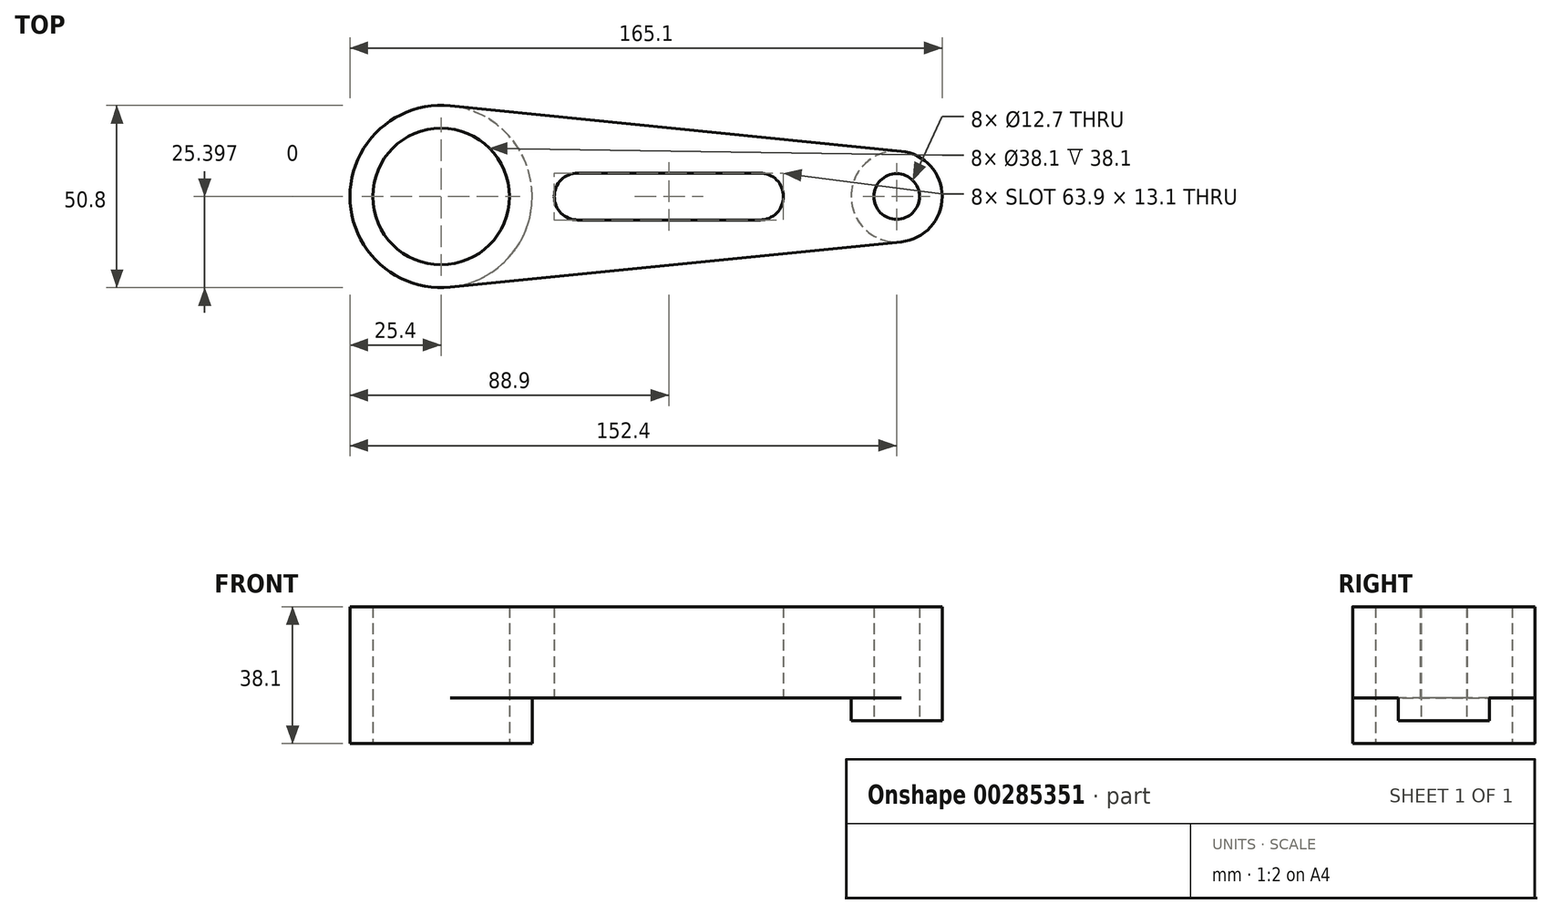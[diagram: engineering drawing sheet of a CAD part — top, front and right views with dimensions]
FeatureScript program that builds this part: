
annotation { "Feature Type Name" : "Feature", "Feature Type Description" : "" }
export const myFeature = defineFeature(function(context is Context, id is Id, definition is map)
    precondition{}
    {
        {
            var Q0;
            Q0=qCreatedBy(makeId("Top.planeOp"),FACE);
            var sketch = newSketch(context, id + "F0", { "sketchPlane" : qUnion([Q0])});
            skCircle(sketch, "E0", {"center": v(-840.18, 447.2) * mm, "radius": 25.4 * mm});
            skCircle(sketch, "E1", {"center": v(-840.18, 447.2) * mm, "radius": 19.05 * mm});
            skCircle(sketch, "E2", {"center": v(-713.18, 447.2) * mm, "radius": 12.7 * mm});
            skCircle(sketch, "E3", {"center": v(-713.18, 447.2) * mm, "radius": 6.35 * mm});
            skLineSegment(sketch, "E4", {"start": v(-837.64, 472.47) * mm, "end": v(-711.9, 459.83) * mm});
            skLineSegment(sketch, "E5", {"start": v(-837.64, 421.92) * mm, "end": v(-711.9, 434.56) * mm});
            skArc(sketch, "E6", {"start": v(-802.08, 453.74) * mm, "mid": v(-808.63, 447.2) * mm, "end": v(-802.08, 440.65) * mm});
            skArc(sketch, "E7", {"start": v(-751.28, 440.65) * mm, "mid": v(-744.73, 447.2) * mm, "end": v(-751.28, 453.74) * mm});
            skLineSegment(sketch, "E8", {"start": v(-802.08, 453.74) * mm, "end": v(-751.28, 453.74) * mm});
            skLineSegment(sketch, "E9", {"start": v(-802.08, 440.65) * mm, "end": v(-751.28, 440.65) * mm});
            skSolve(sketch);
        }
        {
            var Q0;
            Q0 = qSketchRegion(id + "F0", true);
            extrude(context, id + "F1", {"entities" : qUnion([Q0]), "depth" : 38.1 * mm});
        }
        {
            var Q0;
            {var subQ1=sQuery(id+"F0.wireOp",EDGE,"E4");Q0=makeQuery(id+"F0.imprint","IMPRINT",FACE,{"disambiguationData":[TD([[makeQuery(id+"F0.imprint","IMPRINT",EDGE,{"derivedFrom":subQ1}),-1.0]])]});}
            extrude(context, id + "F2", {"entities" : qUnion([Q0]), "operationType" : NewBodyOperationType.REMOVE, "depth" : 12.7 * mm});
        }
        {
            var Q0;
            {var subQ0=sQuery(id+"F0.wireOp",EDGE,"E2");var subQ1=sQuery(id+"F0.wireOp",EDGE,"E3");Q0=makeQuery(id+"F2.boolean.opBoolean","SPLIT",FACE,{"disambiguationData":[TD([makeQuery(id+"F1.opExtrude","SWEPT_FACE",FACE,{"disambiguationData":[OSD([subQ0])]})])],"derivedFrom":makeQuery(id+"F1.opExtrude","CAP_FACE",FACE,{"disambiguationData":[OSD([sQuery(id+"F0.wireOp",EDGE,"E0"),sQuery(id+"F0.wireOp",EDGE,"E1"),subQ0,subQ1,sQuery(id+"F0.wireOp",EDGE,"E4"),sQuery(id+"F0.wireOp",EDGE,"E5"),sQuery(id+"F0.wireOp",EDGE,"E6"),sQuery(id+"F0.wireOp",EDGE,"E7"),sQuery(id+"F0.wireOp",EDGE,"E8"),sQuery(id+"F0.wireOp",EDGE,"E9")])],"isStart":true})});}
            extrude(context, id + "F3", {"entities" : qUnion([Q0]), "operationType" : NewBodyOperationType.REMOVE, "oppositeDirection" : true, "depth" : 6.35 * mm});
        }
    });
